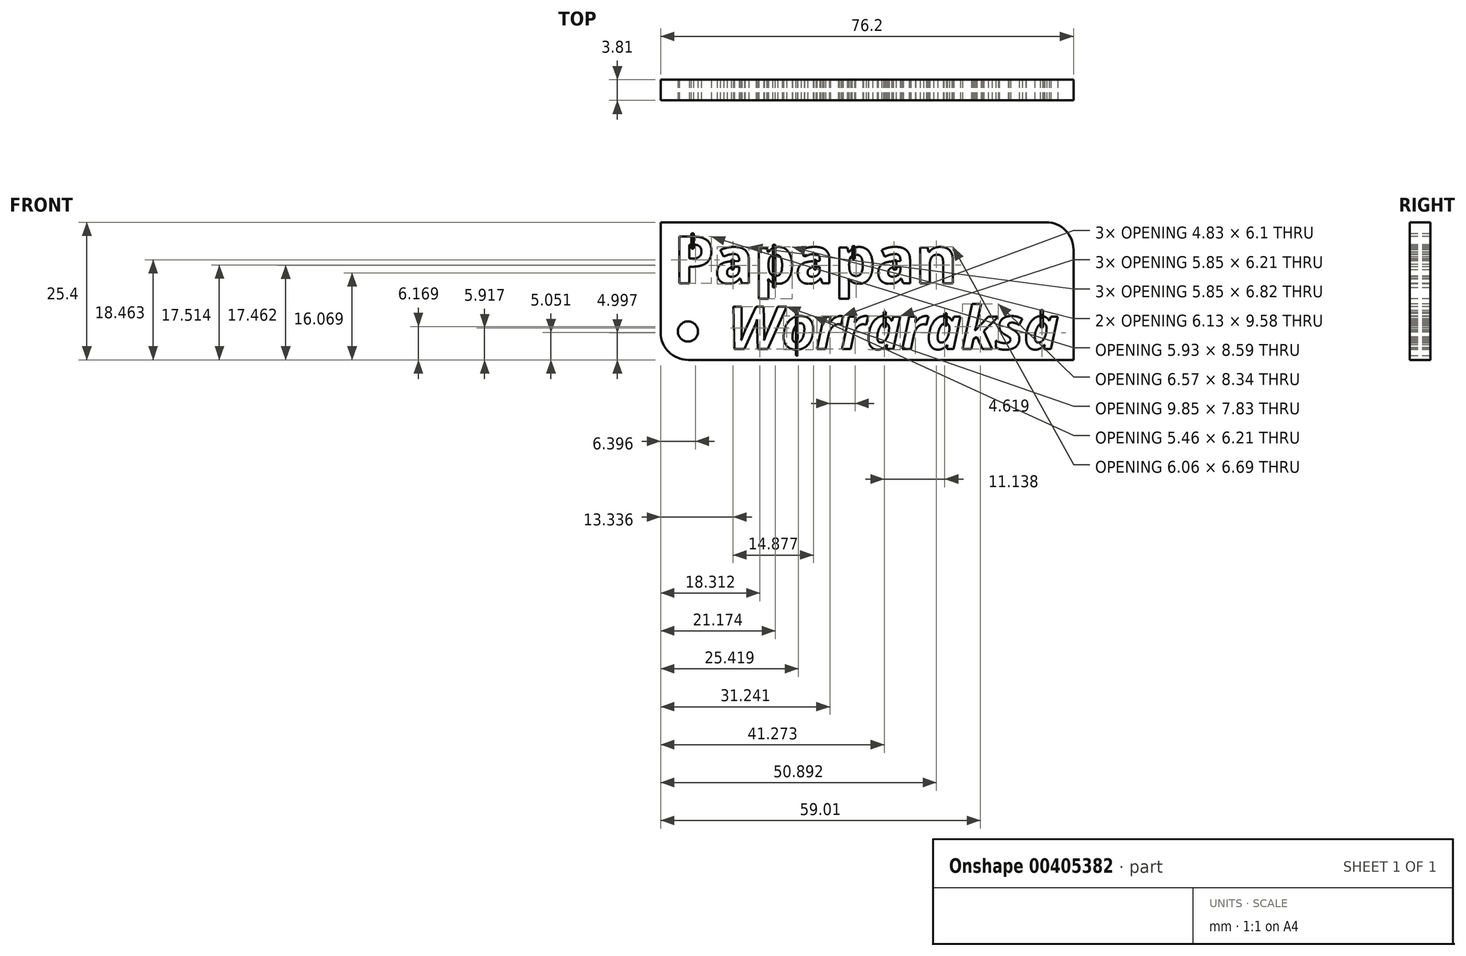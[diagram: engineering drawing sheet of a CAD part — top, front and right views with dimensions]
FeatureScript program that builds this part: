
annotation { "Feature Type Name" : "Feature", "Feature Type Description" : "" }
export const myFeature = defineFeature(function(context is Context, id is Id, definition is map)
    precondition{}
    {
        {
            var Q0;
            Q0=qCreatedBy(makeId("Front.planeOp"),FACE);
            var sketch = newSketch(context, id + "F0", { "sketchPlane" : qUnion([Q0])});
            skLineSegment(sketch, "E0.bottom", {"start": v(0, 0) * mm, "end": v(76.2, 0) * mm});
            skLineSegment(sketch, "E0.top", {"start": v(0, 25.4) * mm, "end": v(76.2, 25.4) * mm});
            skLineSegment(sketch, "E0.left", {"start": v(0, 0) * mm, "end": v(0, 25.4) * mm});
            skLineSegment(sketch, "E0.right", {"start": v(76.2, 0) * mm, "end": v(76.2, 25.4) * mm});
            skSolve(sketch);
        }
        {
            var Q0;
            Q0 = qSketchRegion(id + "F0", true);
            extrude(context, id + "F1", {"entities" : qUnion([Q0]), "depth" : 3.8 * mm});
        }
        {
            var Q0;
            Q0=makeQuery(id+"F1.opExtrude","CAP_FACE",FACE,{"disambiguationData":[OSD([sQuery(id+"F0.wireOp",EDGE,"E0.bottom"),sQuery(id+"F0.wireOp",EDGE,"E0.top"),sQuery(id+"F0.wireOp",EDGE,"E0.left"),sQuery(id+"F0.wireOp",EDGE,"E0.right")])],"isStart":false});
            var sketch = newSketch(context, id + "F2", { "sketchPlane" : qUnion([Q0])});
            skText(sketch, "E1", { "text": "Papapan", "fontName": "OpenSans-Bold.ttf"});
            skText(sketch, "E2", { "text": "Worraraksa", "fontName": "OpenSans-BoldItalic.ttf"});
            const initialGuessF2  = {"E1": [0.00235, 0.01417, 1, 0, 0.00866], "E2": [0.0124, 0.002, 1, 0, 0.0079]};
            skSetInitialGuess(sketch, initialGuessF2);
            skSolve(sketch);
        }
        {
            var Q0;
            Q0 = qSketchRegion(id + "F2", true);
            extrude(context, id + "F3", {"entities" : qUnion([Q0]), "operationType" : NewBodyOperationType.REMOVE, "endBound" : BoundingType.THROUGH_ALL, "oppositeDirection" : true, "depth" : 25.4 * mm});
        }
        {
            var Q0;
            Q0=qCreatedBy(makeId("Front.planeOp"),FACE);
            var sketch = newSketch(context, id + "F4", { "sketchPlane" : qUnion([Q0])});
            skLineSegment(sketch, "E3.bottom", {"start": v(13.11, 18.52) * mm, "end": v(13.5, 18.52) * mm});
            skLineSegment(sketch, "E3.top", {"start": v(13.11, 16.7) * mm, "end": v(13.5, 16.7) * mm});
            skLineSegment(sketch, "E3.left", {"start": v(13.11, 18.52) * mm, "end": v(13.11, 16.7) * mm});
            skLineSegment(sketch, "E3.right", {"start": v(13.5, 18.52) * mm, "end": v(13.5, 16.7) * mm});
            skLineSegment(sketch, "E4.bottom", {"start": v(20.69, 21.25) * mm, "end": v(21.18, 21.25) * mm});
            skLineSegment(sketch, "E4.top", {"start": v(20.69, 13.35) * mm, "end": v(21.18, 13.35) * mm});
            skLineSegment(sketch, "E4.left", {"start": v(20.69, 21.25) * mm, "end": v(20.69, 13.35) * mm});
            skLineSegment(sketch, "E4.right", {"start": v(21.18, 21.25) * mm, "end": v(21.18, 13.35) * mm});
            skLineSegment(sketch, "E5.bottom", {"start": v(28.32, 18.5) * mm, "end": v(28.7, 18.5) * mm});
            skLineSegment(sketch, "E5.top", {"start": v(28.32, 16.7) * mm, "end": v(28.7, 16.7) * mm});
            skLineSegment(sketch, "E5.left", {"start": v(28.32, 18.5) * mm, "end": v(28.32, 16.7) * mm});
            skLineSegment(sketch, "E5.right", {"start": v(28.7, 18.5) * mm, "end": v(28.7, 16.7) * mm});
            skLineSegment(sketch, "E6.bottom", {"start": v(35.36, 20.99) * mm, "end": v(35.8, 20.99) * mm});
            skLineSegment(sketch, "E6.top", {"start": v(35.36, 18.64) * mm, "end": v(35.8, 18.64) * mm});
            skLineSegment(sketch, "E6.left", {"start": v(35.36, 20.99) * mm, "end": v(35.36, 18.64) * mm});
            skLineSegment(sketch, "E6.right", {"start": v(35.8, 20.99) * mm, "end": v(35.8, 18.64) * mm});
            skLineSegment(sketch, "E7.bottom", {"start": v(42.94, 18.37) * mm, "end": v(43.5, 18.37) * mm});
            skLineSegment(sketch, "E7.top", {"start": v(42.94, 16.7) * mm, "end": v(43.5, 16.7) * mm});
            skLineSegment(sketch, "E7.left", {"start": v(42.94, 18.37) * mm, "end": v(42.94, 16.7) * mm});
            skLineSegment(sketch, "E7.right", {"start": v(43.5, 18.37) * mm, "end": v(43.5, 16.7) * mm});
            skLineSegment(sketch, "E8.bottom", {"start": v(25.3, 8.7) * mm, "end": v(24.94, 8.7) * mm});
            skLineSegment(sketch, "E8.top", {"start": v(25.3, 0.84) * mm, "end": v(24.94, 0.84) * mm});
            skLineSegment(sketch, "E8.left", {"start": v(25.3, 8.7) * mm, "end": v(25.3, 0.84) * mm});
            skLineSegment(sketch, "E8.right", {"start": v(24.94, 8.7) * mm, "end": v(24.94, 0.84) * mm});
            skLineSegment(sketch, "E9.bottom", {"start": v(41.56, 8.85) * mm, "end": v(41.15, 8.85) * mm});
            skLineSegment(sketch, "E9.top", {"start": v(41.56, 6) * mm, "end": v(41.15, 6) * mm});
            skLineSegment(sketch, "E9.left", {"start": v(41.56, 8.85) * mm, "end": v(41.56, 6) * mm});
            skLineSegment(sketch, "E9.right", {"start": v(41.15, 8.85) * mm, "end": v(41.15, 6) * mm});
            skLineSegment(sketch, "E10.bottom", {"start": v(52.8, 8.62) * mm, "end": v(52.36, 8.62) * mm});
            skLineSegment(sketch, "E10.top", {"start": v(52.8, 6.36) * mm, "end": v(52.36, 6.36) * mm});
            skLineSegment(sketch, "E10.left", {"start": v(52.8, 8.62) * mm, "end": v(52.8, 6.36) * mm});
            skLineSegment(sketch, "E10.right", {"start": v(52.36, 8.62) * mm, "end": v(52.36, 6.36) * mm});
            skLineSegment(sketch, "E11.bottom", {"start": v(70.56, 9.2) * mm, "end": v(70.15, 9.2) * mm});
            skLineSegment(sketch, "E11.top", {"start": v(70.56, 6) * mm, "end": v(70.15, 6) * mm});
            skLineSegment(sketch, "E11.left", {"start": v(70.56, 9.2) * mm, "end": v(70.56, 6) * mm});
            skLineSegment(sketch, "E11.right", {"start": v(70.15, 9.2) * mm, "end": v(70.15, 6) * mm});
            skLineSegment(sketch, "E12.bottom", {"start": v(5.64, 23.32) * mm, "end": v(6.08, 23.32) * mm});
            skLineSegment(sketch, "E12.top", {"start": v(5.64, 20.57) * mm, "end": v(6.08, 20.57) * mm});
            skLineSegment(sketch, "E12.left", {"start": v(5.64, 23.32) * mm, "end": v(5.64, 20.57) * mm});
            skLineSegment(sketch, "E12.right", {"start": v(6.08, 23.32) * mm, "end": v(6.08, 20.57) * mm});
            skSolve(sketch);
        }
        {
            var Q0;
            Q0 = qSketchRegion(id + "F4", true);
            extrude(context, id + "F5", {"entities" : qUnion([Q0]), "depth" : 3.8 * mm});
        }
        {
            var Q0;
            {var subQ0=sQuery(id+"F0.wireOp",EDGE,"E0.bottom");var subQ1=sQuery(id+"F0.wireOp",EDGE,"E0.right");var subQ2=sQuery(id+"F0.wireOp",EDGE,"E0.top");var subQ3=sQuery(id+"F0.wireOp",EDGE,"E0.left");Q0=makeQuery(id+"F3.boolean.opBoolean","SPLIT",FACE,{"disambiguationData":[TD([makeQuery(id+"F1.opExtrude","SWEPT_FACE",FACE,{"disambiguationData":[OSD([subQ0])]})])],"derivedFrom":makeQuery(id+"F1.opExtrude","CAP_FACE",FACE,{"disambiguationData":[OSD([subQ0,subQ2,subQ3,subQ1])],"isStart":false})});}
            var sketch = newSketch(context, id + "F6", { "sketchPlane" : qUnion([Q0])});
            skCircle(sketch, "E13", {"center": v(5.03, 5.25) * mm, "radius": 1.85 * mm});
            skSolve(sketch);
        }
        {
            var Q0;
            Q0 = qSketchRegion(id + "F6", true);
            extrude(context, id + "F7", {"entities" : qUnion([Q0]), "operationType" : NewBodyOperationType.REMOVE, "endBound" : BoundingType.THROUGH_ALL, "oppositeDirection" : true, "depth" : 25.4 * mm});
        }
        {
            var Q0;
            Q0=makeQuery(id+"F1.opExtrude","SWEPT_EDGE",EDGE,{"disambiguationData":[OSD([sQuery(id+"F0.wireOp",EDGE,"E0.bottom"),sQuery(id+"F0.wireOp",EDGE,"E0.left")])]});
            fillet(context, id + "F8", {"entities" : qUnion([Q0]), "radius" : 5.08 * mm, "tangentPropagation" : true, "allowEdgeOverflow" : false});
        }
        {
            var Q0;
            Q0=makeQuery(id+"F1.opExtrude","SWEPT_EDGE",EDGE,{"disambiguationData":[OSD([sQuery(id+"F0.wireOp",EDGE,"E0.top"),sQuery(id+"F0.wireOp",EDGE,"E0.right")])]});
            fillet(context, id + "F9", {"entities" : qUnion([Q0]), "radius" : 5.08 * mm, "tangentPropagation" : true, "allowEdgeOverflow" : false});
        }
    });
